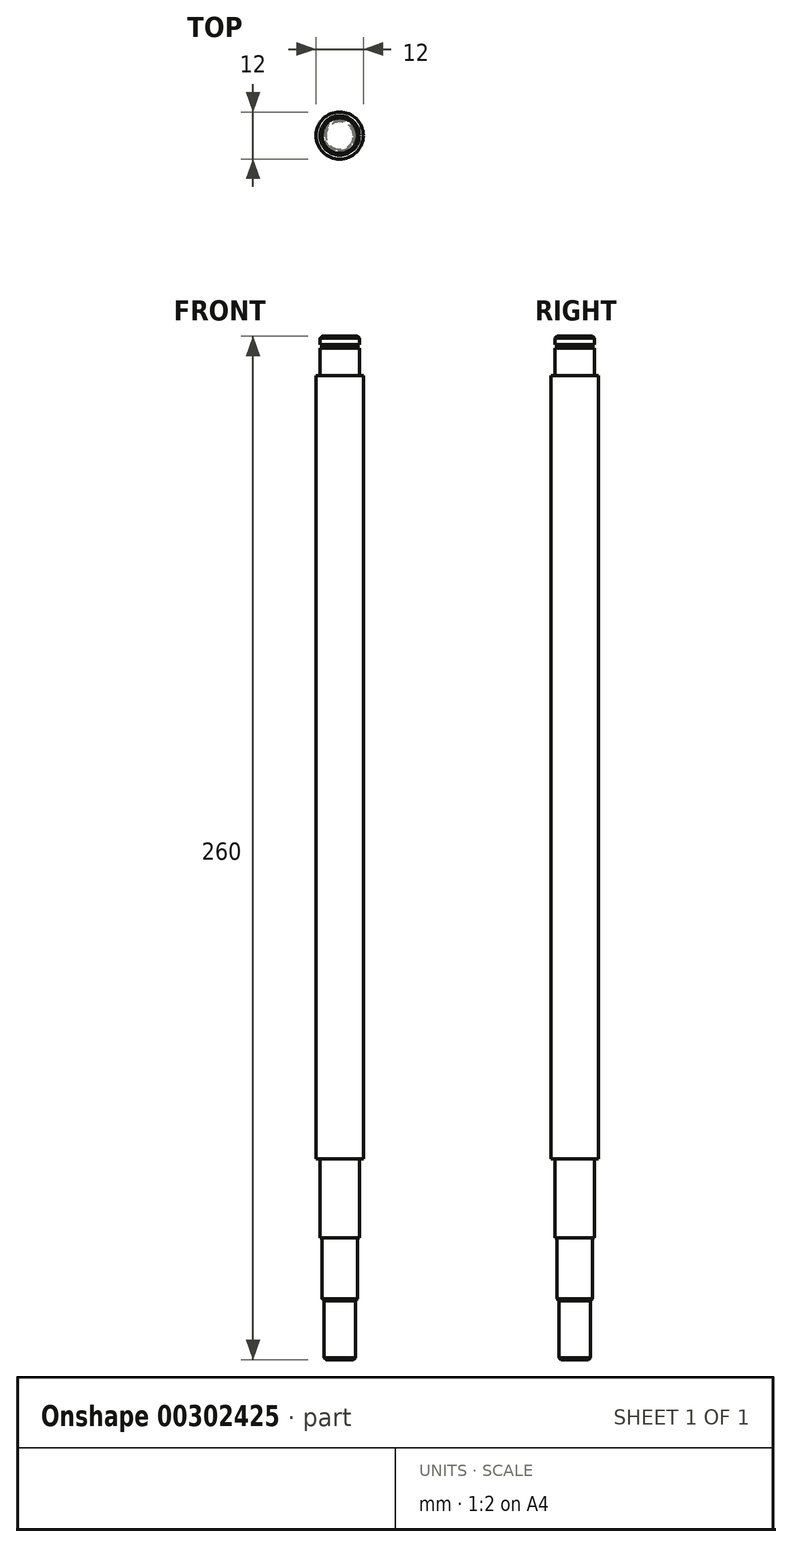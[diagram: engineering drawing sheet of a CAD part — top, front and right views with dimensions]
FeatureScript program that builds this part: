
annotation { "Feature Type Name" : "Feature", "Feature Type Description" : "" }
export const myFeature = defineFeature(function(context is Context, id is Id, definition is map)
    precondition{}
    {
        {
            var Q0;
            Q0=qCreatedBy(makeId("Front.planeOp"),FACE);
            var sketch = newSketch(context, id + "F0", { "sketchPlane" : qUnion([Q0])});
            skLineSegment(sketch, "E0", {"start": v(0, 0) * mm, "end": v(0, 285.84) * mm, "construction": true});
            skLineSegment(sketch, "E1", {"start": v(0, 0) * mm, "end": v(3.5, 0) * mm});
            skLineSegment(sketch, "E2", {"start": v(3.5, 0) * mm, "end": v(4, 0.5) * mm});
            skLineSegment(sketch, "E3", {"start": v(4, 0.5) * mm, "end": v(4, 15) * mm});
            skLineSegment(sketch, "E4", {"start": v(4, 15) * mm, "end": v(4.5, 15.5) * mm});
            skLineSegment(sketch, "E5", {"start": v(4.5, 15.5) * mm, "end": v(4.5, 31) * mm});
            skLineSegment(sketch, "E6", {"start": v(4.5, 31) * mm, "end": v(5, 31) * mm});
            skLineSegment(sketch, "E7", {"start": v(5, 31) * mm, "end": v(5, 51) * mm});
            skLineSegment(sketch, "E8", {"start": v(5, 51) * mm, "end": v(6, 51) * mm});
            skLineSegment(sketch, "E9", {"start": v(6, 51) * mm, "end": v(6, 250) * mm});
            skLineSegment(sketch, "E10", {"start": v(6, 250) * mm, "end": v(5, 250) * mm});
            skLineSegment(sketch, "E11", {"start": v(5, 250) * mm, "end": v(5, 257) * mm});
            skLineSegment(sketch, "E12", {"start": v(5, 257) * mm, "end": v(3.8, 257) * mm});
            skLineSegment(sketch, "E13", {"start": v(3.8, 257) * mm, "end": v(3.8, 257.9) * mm});
            skLineSegment(sketch, "E14", {"start": v(3.8, 257.9) * mm, "end": v(5, 257.9) * mm});
            skLineSegment(sketch, "E15", {"start": v(5, 257.9) * mm, "end": v(5, 259.5) * mm});
            skLineSegment(sketch, "E16", {"start": v(5, 259.5) * mm, "end": v(4.5, 260) * mm});
            skLineSegment(sketch, "E17", {"start": v(4.5, 260) * mm, "end": v(0, 260) * mm});
            skLineSegment(sketch, "E18", {"start": v(0, 260) * mm, "end": v(0, 0) * mm});
            skSolve(sketch);
        }
        {
            var Q0;
            Q0=qSketchRegion(id+"F0",true);
            var Q1;
            Q1=sQuery(id+"F0.wireOp",EDGE,"E0");
            revolve(context, id + "F1", {"entities" : qUnion([Q0]), "axis" : qUnion([Q1]), "revolveType" : RevolveType.FULL});
        }
    });
